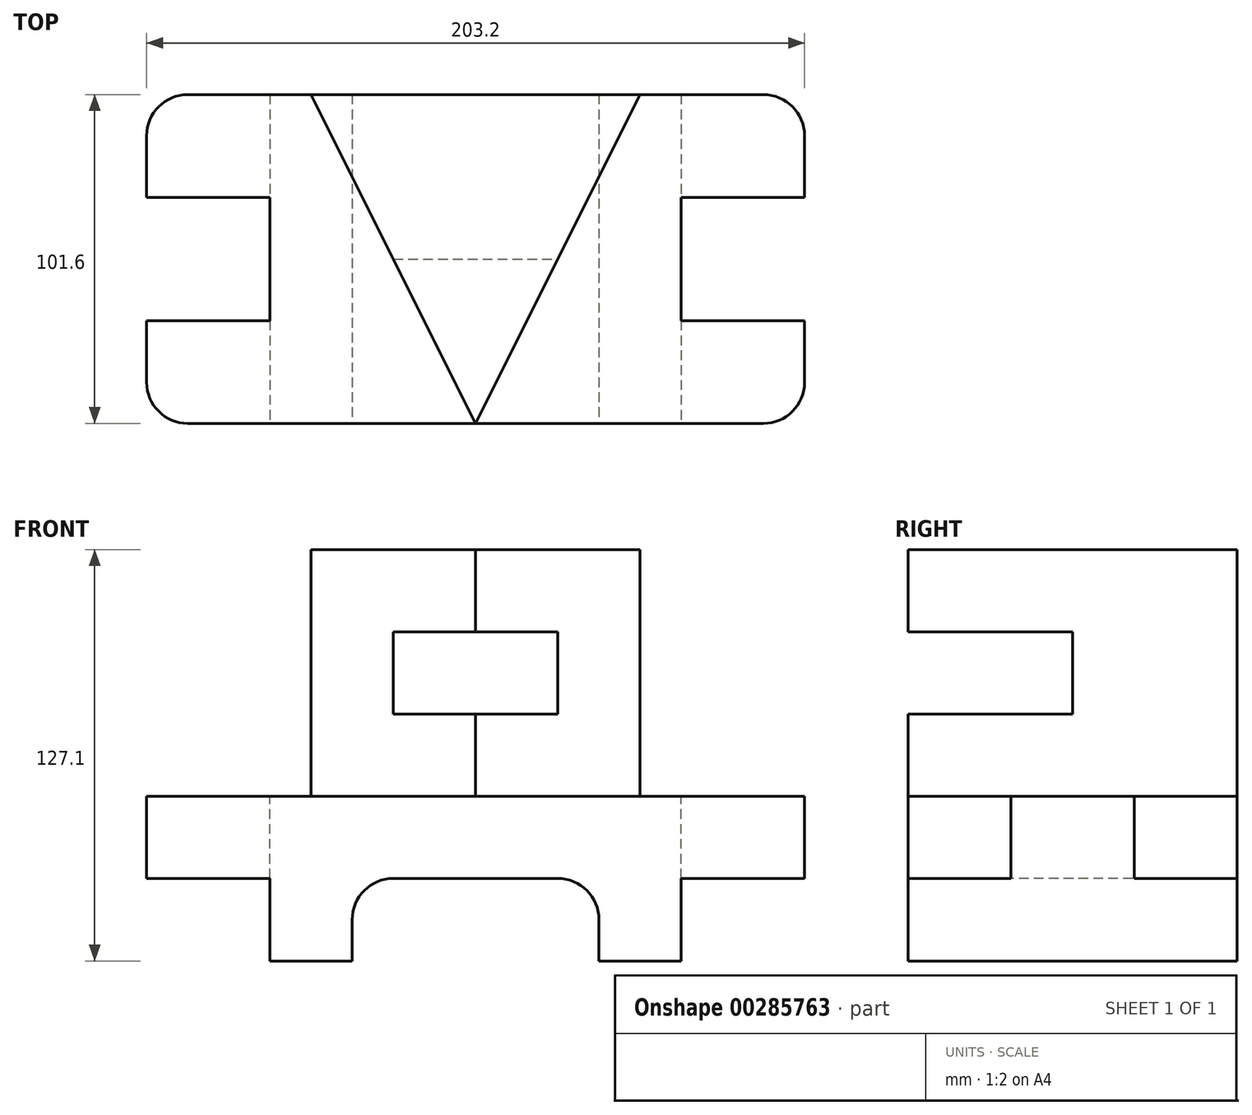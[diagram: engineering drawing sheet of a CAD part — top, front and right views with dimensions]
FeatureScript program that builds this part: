
annotation { "Feature Type Name" : "Feature", "Feature Type Description" : "" }
export const myFeature = defineFeature(function(context is Context, id is Id, definition is map)
    precondition{}
    {
        {
            var Q0;
            Q0=qCreatedBy(makeId("Top.planeOp"),FACE);
            var sketch = newSketch(context, id + "F0", { "sketchPlane" : qUnion([Q0])});
            skLineSegment(sketch, "E0", {"start": v(0, 0) * mm, "end": v(50.8, 101.6) * mm});
            skLineSegment(sketch, "E1", {"start": v(50.8, 101.6) * mm, "end": v(-50.8, 101.6) * mm});
            skLineSegment(sketch, "E2", {"start": v(-50.8, 101.6) * mm, "end": v(0, 0) * mm});
            skSolve(sketch);
        }
        {
            var Q0;
            Q0 = qSketchRegion(id + "F0", true);
            extrude(context, id + "F1", {"entities" : qUnion([Q0]), "depth" : 76.2 * mm});
        }
        {
            var Q0;
            Q0=qCreatedBy(makeId("Right.planeOp"),FACE);
            var sketch = newSketch(context, id + "F2", { "sketchPlane" : qUnion([Q0])});
            skLineSegment(sketch, "E3.bottom", {"start": v(0, 50.8) * mm, "end": v(50.8, 50.8) * mm});
            skLineSegment(sketch, "E3.top", {"start": v(0, 25.4) * mm, "end": v(50.8, 25.4) * mm});
            skLineSegment(sketch, "E3.left", {"start": v(0, 50.8) * mm, "end": v(0, 25.4) * mm});
            skLineSegment(sketch, "E3.right", {"start": v(50.8, 50.8) * mm, "end": v(50.8, 25.4) * mm});
            skSolve(sketch);
        }
        {
            var Q0;
            Q0 = qSketchRegion(id + "F2", true);
            extrude(context, id + "F3", {"entities" : qUnion([Q0]), "operationType" : NewBodyOperationType.REMOVE, "endBound" : BoundingType.THROUGH_ALL, "oppositeDirection" : true, "depth" : 25.4 * mm, "hasSecondDirection" : true, "secondDirectionBound" : SecondDirectionBoundingType.THROUGH_ALL, "secondDirectionOppositeDirection" : false, "secondDirectionDepth" : 25.4 * mm});
        }
        {
            var Q0;
            Q0=makeQuery(id+"F1.opExtrude","CAP_FACE",FACE,{"disambiguationData":[OSD([sQuery(id+"F0.wireOp",EDGE,"E0"),sQuery(id+"F0.wireOp",EDGE,"E1"),sQuery(id+"F0.wireOp",EDGE,"E2")])],"isStart":true});
            var sketch = newSketch(context, id + "F4", { "sketchPlane" : qUnion([Q0])});
            skLineSegment(sketch, "E4.bottom", {"start": v(101.6, -31.75) * mm, "end": v(63.5, -31.75) * mm});
            skLineSegment(sketch, "E4.top", {"start": v(101.6, -69.85) * mm, "end": v(63.5, -69.85) * mm});
            skLineSegment(sketch, "E4.right", {"start": v(63.5, -31.75) * mm, "end": v(63.5, -69.85) * mm});
            skLineSegment(sketch, "E5.bottom", {"start": v(-101.6, -31.75) * mm, "end": v(-63.5, -31.75) * mm});
            skLineSegment(sketch, "E5.top", {"start": v(-101.6, -69.85) * mm, "end": v(-63.5, -69.85) * mm});
            skLineSegment(sketch, "E5.right", {"start": v(-63.5, -31.75) * mm, "end": v(-63.5, -69.85) * mm});
            skPoint(sketch, "E6.oppositeSnap0", {"position": v(-101.6, -12.7) * mm});
            skPoint(sketch, "E7.oppositeSnap0", {"position": v(101.6, -88.9) * mm});
            skArc(sketch, "E8", {"start": v(101.6, -12.7) * mm, "mid": v(97.88, -3.72) * mm, "end": v(88.9, 0) * mm});
            skArc(sketch, "E9", {"start": v(-88.9, 0) * mm, "mid": v(-97.88, -3.72) * mm, "end": v(-101.6, -12.7) * mm});
            skArc(sketch, "E10", {"start": v(-101.6, -88.9) * mm, "mid": v(-97.88, -97.88) * mm, "end": v(-88.9, -101.6) * mm});
            skArc(sketch, "E11", {"start": v(88.9, -101.6) * mm, "mid": v(97.88, -97.88) * mm, "end": v(101.6, -88.9) * mm});
            skLineSegment(sketch, "E12", {"start": v(-88.9, 0) * mm, "end": v(88.9, 0) * mm});
            skLineSegment(sketch, "E13", {"start": v(101.6, -12.7) * mm, "end": v(101.6, -31.75) * mm});
            skLineSegment(sketch, "E14", {"start": v(-101.6, -88.9) * mm, "end": v(-101.6, -69.85) * mm});
            skLineSegment(sketch, "E15", {"start": v(-101.6, -31.75) * mm, "end": v(-101.6, -12.7) * mm});
            skLineSegment(sketch, "E16", {"start": v(-88.9, -101.6) * mm, "end": v(88.9, -101.6) * mm});
            skLineSegment(sketch, "E17", {"start": v(101.6, -69.85) * mm, "end": v(101.6, -88.9) * mm});
            skLineSegment(sketch, "E18", {"start": v(-50.8, -101.6) * mm, "end": v(50.8, -101.6) * mm});
            skSolve(sketch);
        }
        {
            var Q0;
            Q0 = qSketchRegion(id + "F4", true);
            extrude(context, id + "F5", {"entities" : qUnion([Q0]), "operationType" : NewBodyOperationType.ADD, "depth" : 25.4 * mm});
        }
        {
            var Q0;
            Q0 = qSketchRegion(id + "F4", true);
            extrude(context, id + "F6", {"entities" : qUnion([Q0]), "operationType" : NewBodyOperationType.ADD, "depth" : 25.4 * mm});
        }
        {
            var Q0;
            Q0=makeQuery(id+"F5.opExtrude","SWEPT_FACE",FACE,{"disambiguationData":[OSD([sQuery(id+"F4.wireOp",EDGE,"E12")])]});
            var sketch = newSketch(context, id + "F7", { "sketchPlane" : qUnion([Q0])});
            skLineSegment(sketch, "E19", {"start": v(-63.5, -25.4) * mm, "end": v(-63.5, -50.9) * mm});
            skLineSegment(sketch, "E20", {"start": v(-63.5, -50.9) * mm, "end": v(-38.1, -50.9) * mm});
            skLineSegment(sketch, "E21", {"start": v(-63.5, -25.4) * mm, "end": v(63.5, -25.4) * mm});
            skLineSegment(sketch, "E22", {"start": v(63.5, -25.4) * mm, "end": v(63.5, -50.9) * mm});
            skLineSegment(sketch, "E23", {"start": v(63.5, -50.9) * mm, "end": v(38.1, -50.9) * mm});
            skLineSegment(sketch, "E24", {"start": v(-38.1, -50.9) * mm, "end": v(-38.1, -25.4) * mm});
            skLineSegment(sketch, "E25", {"start": v(38.1, -50.9) * mm, "end": v(38.1, -25.4) * mm});
            skSolve(sketch);
        }
        {
            var Q0;
            Q0 = qSketchRegion(id + "F7", true);
            extrude(context, id + "F8", {"entities" : qUnion([Q0]), "operationType" : NewBodyOperationType.ADD, "oppositeDirection" : true, "depth" : 101.6 * mm});
        }
        {
            var Q0;
            Q0=makeQuery(id+"F8.opExtrude","SWEPT_EDGE",EDGE,{"disambiguationData":[OSD([sQuery(id+"F7.wireOp",EDGE,"E21"),sQuery(id+"F7.wireOp",EDGE,"E24")])]});
            var Q1;
            Q1=makeQuery(id+"F8.opExtrude","SWEPT_EDGE",EDGE,{"disambiguationData":[OSD([sQuery(id+"F7.wireOp",EDGE,"E21"),sQuery(id+"F7.wireOp",EDGE,"E25")])]});
            fillet(context, id + "F9", {"entities" : qUnion([Q0, Q1]), "radius" : 12.7 * mm, "tangentPropagation" : true, "allowEdgeOverflow" : false});
        }
    });
